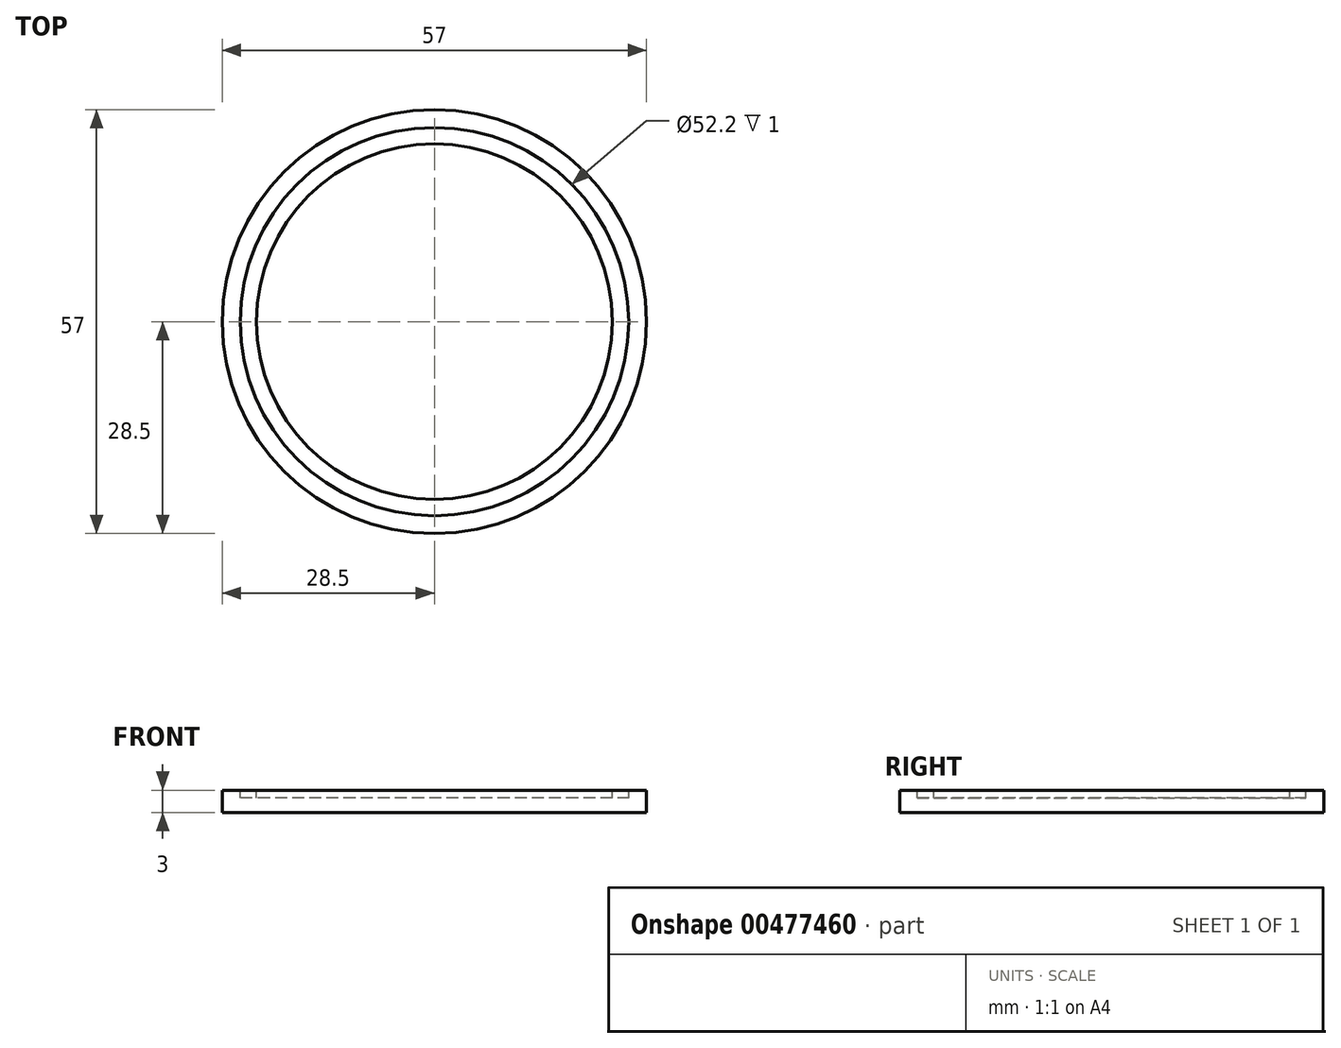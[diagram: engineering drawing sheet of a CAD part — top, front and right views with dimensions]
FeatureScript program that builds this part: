
annotation { "Feature Type Name" : "Feature", "Feature Type Description" : "" }
export const myFeature = defineFeature(function(context is Context, id is Id, definition is map)
    precondition{}
    {
        {
            var Q0;
            Q0=qCreatedBy(makeId("Top.planeOp"),FACE);
            var sketch = newSketch(context, id + "F0", { "sketchPlane" : qUnion([Q0])});
            skCircle(sketch, "E0", {"center": v(0, 0) * mm, "radius": 28.5 * mm});
            skSolve(sketch);
        }
        {
            var Q0;
            Q0 = qSketchRegion(id + "F0", true);
            extrude(context, id + "F1", {"entities" : qUnion([Q0]), "depth" : 3 * mm});
        }
        {
            var Q0;
            Q0=makeQuery(id+"F1.opExtrude","CAP_FACE",FACE,{"disambiguationData":[OSD([sQuery(id+"F0.wireOp",EDGE,"E0")])],"isStart":false});
            var sketch = newSketch(context, id + "F2", { "sketchPlane" : qUnion([Q0])});
            skCircle(sketch, "E1", {"center": v(0, 0) * mm, "radius": 26.1 * mm});
            skCircle(sketch, "E2", {"center": v(0, 0) * mm, "radius": 23.9 * mm});
            skSolve(sketch);
        }
        {
            var Q0;
            Q0 = qSketchRegion(id + "F2", true);
            extrude(context, id + "F3", {"entities" : qUnion([Q0]), "operationType" : NewBodyOperationType.REMOVE, "oppositeDirection" : true, "depth" : 1 * mm});
        }
    });
